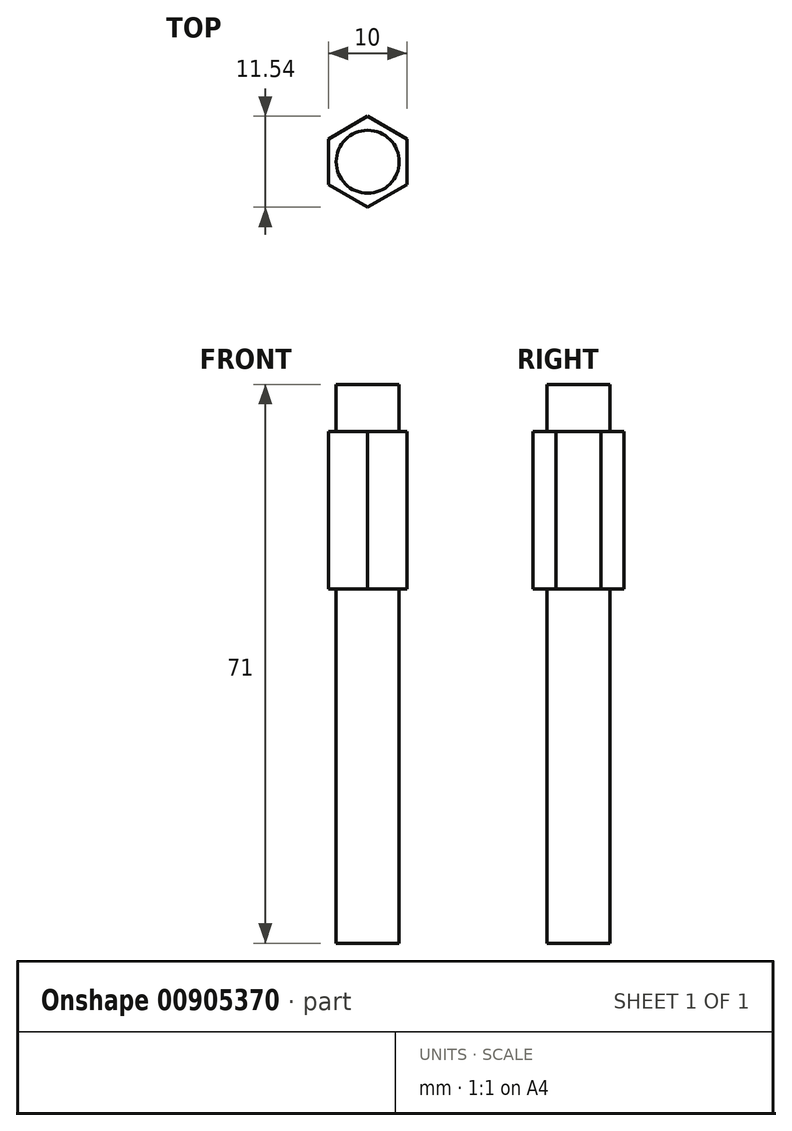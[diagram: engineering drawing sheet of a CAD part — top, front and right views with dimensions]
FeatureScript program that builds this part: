
annotation { "Feature Type Name" : "Feature", "Feature Type Description" : "" }
export const myFeature = defineFeature(function(context is Context, id is Id, definition is map)
    precondition{}
    {
        {
            var Q0;
            Q0=qCreatedBy(makeId("Top.planeOp"),FACE);
            var sketch = newSketch(context, id + "F0", { "sketchPlane" : qUnion([Q0])});
            skCircle(sketch, "E0.cCircle", {"center": v(0, 0) * mm, "radius": 5.77 * mm, "construction": true});
            skLineSegment(sketch, "E0.0", {"start": v(0, 5.77) * mm, "end": v(5, 2.89) * mm});
            skLineSegment(sketch, "E0.1", {"start": v(5, 2.89) * mm, "end": v(5, -2.89) * mm});
            skLineSegment(sketch, "E0.2", {"start": v(5, -2.89) * mm, "end": v(0, -5.77) * mm});
            skLineSegment(sketch, "E0.3", {"start": v(0, -5.77) * mm, "end": v(-5, -2.89) * mm});
            skLineSegment(sketch, "E0.4", {"start": v(-5, -2.89) * mm, "end": v(-5, 2.89) * mm});
            skLineSegment(sketch, "E0.5", {"start": v(-5, 2.89) * mm, "end": v(0, 5.77) * mm});
            skSolve(sketch);
        }
        {
            var Q0;
            Q0=makeQuery(id+"F0.imprint","IMPRINT",FACE,{"disambiguationData":[TD([[makeQuery(id+"F0.imprint","IMPRINT",EDGE,{"derivedFrom":sQuery(id+"F0.wireOp",EDGE,"E0.0")}),-1.0]])]});
            extrude(context, id + "F1", {"entities" : qUnion([Q0]), "depth" : 20 * mm, "offsetDistance" : 25 * mm});
        }
        {
            var Q0;
            Q0=makeQuery(id+"F1.opExtrude","CAP_FACE",FACE,{"disambiguationData":[OSD([sQuery(id+"F0.wireOp",EDGE,"E0.0"),sQuery(id+"F0.wireOp",EDGE,"E0.1"),sQuery(id+"F0.wireOp",EDGE,"E0.2"),sQuery(id+"F0.wireOp",EDGE,"E0.3"),sQuery(id+"F0.wireOp",EDGE,"E0.4"),sQuery(id+"F0.wireOp",EDGE,"E0.5")])],"isStart":true});
            var sketch = newSketch(context, id + "F2", { "sketchPlane" : qUnion([Q0])});
            skCircle(sketch, "E1", {"center": v(0, 0) * mm, "radius": 4 * mm});
            skSolve(sketch);
        }
        {
            var Q0;
            Q0=qSketchRegion(id+"F2",true);
            extrude(context, id + "F3", {"entities" : qUnion([Q0]), "operationType" : NewBodyOperationType.ADD, "depth" : 45 * mm, "offsetDistance" : 25 * mm});
        }
        {
            var Q0;
            Q0=makeQuery(id+"F1.opExtrude","CAP_FACE",FACE,{"disambiguationData":[OSD([sQuery(id+"F0.wireOp",EDGE,"E0.0"),sQuery(id+"F0.wireOp",EDGE,"E0.1"),sQuery(id+"F0.wireOp",EDGE,"E0.2"),sQuery(id+"F0.wireOp",EDGE,"E0.3"),sQuery(id+"F0.wireOp",EDGE,"E0.4"),sQuery(id+"F0.wireOp",EDGE,"E0.5")])],"isStart":false});
            var sketch = newSketch(context, id + "F4", { "sketchPlane" : qUnion([Q0])});
            skCircle(sketch, "E2", {"center": v(0, 0) * mm, "radius": 4 * mm});
            skSolve(sketch);
        }
        {
            var Q0;
            Q0=qSketchRegion(id+"F4",true);
            extrude(context, id + "F5", {"entities" : qUnion([Q0]), "operationType" : NewBodyOperationType.ADD, "depth" : 6 * mm, "offsetDistance" : 25 * mm});
        }
    });
